SOLIDWORKS PART (.sldprt)
format: sldprt  version: not decoded by parser v0  size: 663,552 bytes
history: native  units: mm
features: plane x3, sketch x3, extrude x2, chamfer x2, material x1, cut_extrude x1 + 1 further entry (+8 scaffold rows collapsed)
feature tree (21):
  scaffold x8  (default folders/planes/origin — collapsed)
  material  "Matériau <non spécifié>"
  "Corps de surface"
  plane  "Face"
  plane  "Dessus"
  plane  "Droite"
  sketch  "Esquisse1"  dims[c1.D1=~10.638828mm c1.D2=0.15mm c1.D3=0.15mm c1.D4=0.15mm c1.D5=0.15mm c1.D6=0.15mm c1.D7=0.15mm c2.D1=~0.604849mm c3.D1=20.0deg]
  extrude  "Base-Extrusion"  Depth=1.5mm
  sketch  "Esquisse2"  dims[D1=~1.542471mm]
  extrude  "Boss.-Extru.1"  Depth=6mm
  sketch  "Esquisse3"  dims[D1=~1.509299mm]
  cut_extrude  "Enlèv. mat.-Extru.1"  Depth=10mm
  chamfer  "Chanfrein1"  Distance=0.3mm Angle=45deg
  chamfer  "Dépouille2"  Angle=2deg  [1 undecoded]
decode coverage: 8 of 8 modeling features carry decoded parameters; 1 rows unclassified (native names shown)
note: ~ marks probable driven/reference dimensions
note: 1 parameter value undecoded
note: suppression state not decoded; provenance and decode notes live in map.json
